# Revit family: Floor_Door-Best-Access-Doors-Flush_Floodtight_Gastight-BA-GTFD_Series
name_source: partatom
category: Specialty Equipment
revit_build: Autodesk Revit 2017 (Build: 20160225_1515(x64)
units: mm (PartAtom-declared; Revit-internal decimal feet)

## family parameters
Cut with Voids When Loaded = Yes
Host = Face
OmniClass Number = 23.40.00.00
Part Type = Normal
Room Calculation Point = No
Round Connector Dimension = Use Diameter
Shared = Yes

## types (8) — shared parameters
Assembly Code = C1020700
Description = BA-GTFD - Floodtight/Gastight Floor Door
Finish = Aluminum-Best-Access-Doors-Satin
Installation Type = Floor
Label = Access Door
Length = 3 3/4"
Manufacturer = Best Access Doors
Material = Aluminum-Best-Access-Doors-Satin
Product data url = https://bimobject.com
Standard Cam Latch = Yes
URL = https://www.bestaccessdoors.com

## per-type parameters (varying)
| type | Default Elevation | Height | Shipping Weight | Width |
| BA-GTFD 24x24 | 0" | 24" | 75 lb | 24" |
| BA-GTFD 24x36 | 48" | 36" | 100 lb | 24" |
| BA-GTFD 30x30 | 48" | 30" | 105 lb | 30" |
| BA-GTFD 30x36 | 48" | 36" | 115 lb | 30" |
| BA-GTFD 36x36 | 48" | 36" | 130 lb | 36" |
| BA-GTFD 36x48 | 48" | 48" | 155 lb | 36" |
| BA-GTFD 24x30 | 48" | 30" | 90 lb | 24" |
| BA-GTFD 30x48 | 48" | 48" | 140 lb | 30" |

note: column(s) folded — value = type name in every type: Model

## geometry (parser evidence)
native form markers: Sweep x1
no freeform markers — native parametric forms only
